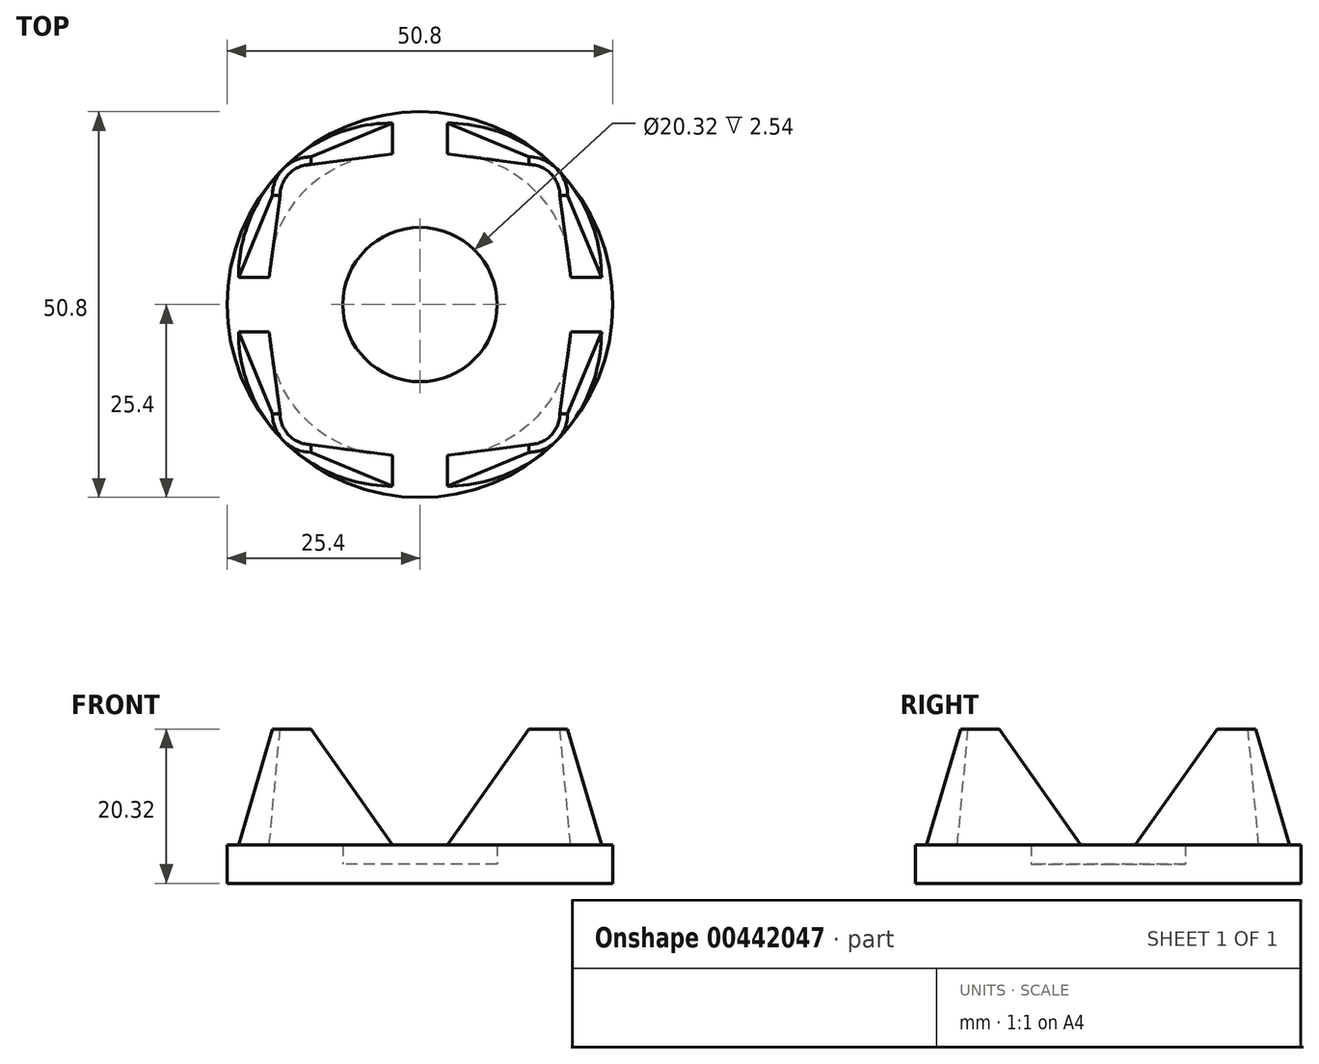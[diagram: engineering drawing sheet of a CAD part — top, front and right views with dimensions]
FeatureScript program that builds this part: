
annotation { "Feature Type Name" : "Feature", "Feature Type Description" : "" }
export const myFeature = defineFeature(function(context is Context, id is Id, definition is map)
    precondition{}
    {
        {
            var Q0;
            Q0=qCreatedBy(makeId("Top.planeOp"),FACE);
            var sketch = newSketch(context, id + "F0", { "sketchPlane" : qUnion([Q0])});
            skCircle(sketch, "E0", {"center": v(0, 0) * mm, "radius": 25.4 * mm});
            skCircle(sketch, "E1", {"center": v(0, 0) * mm, "radius": 10.16 * mm});
            skCircle(sketch, "E2.0", {"center": v(0, 0) * mm, "radius": 20.32 * mm});
            skLineSegment(sketch, "E3", {"start": v(0, 0) * mm, "end": v(0, 25.4) * mm});
            skLineSegment(sketch, "E4", {"start": v(0, 0) * mm, "end": v(-25.4, 0) * mm});
            skLineSegment(sketch, "E5", {"start": v(0, 0) * mm, "end": v(0, -25.4) * mm});
            skLineSegment(sketch, "E6", {"start": v(0, 0) * mm, "end": v(25.4, 0) * mm});
            skSolve(sketch);
        }
        {
            var Q0;
            Q0=makeQuery(id+"F0.imprint","IMPRINT",FACE,{"disambiguationData":[TD([[makeQuery(id+"F0.imprint","IMPRINT",EDGE,{"derivedFrom":sQuery(id+"F0.wireOp",EDGE,"E0")}),1.0]])]});
            var Q1;
            {var subQ0=sQuery(id+"F0.wireOp",EDGE,"E3");var subQ1=sQuery(id+"F0.wireOp",EDGE,"E2.0");var subQ2=makeQuery(id+"F0.imprint","INTERSECT",VERTEX,{"derivedFrom":[subQ1,subQ0]});Q1=makeQuery(id+"F0.imprint","IMPRINT",FACE,{"disambiguationData":[TD([[makeQuery(id+"F0.imprint","IMPRINT",EDGE,{"disambiguationData":[TD([[subQ2,-1.0]])],"derivedFrom":subQ1}),1.0]])]});}
            var Q2;
            {var subQ0=sQuery(id+"F0.wireOp",EDGE,"E3");var subQ1=sQuery(id+"F0.wireOp",EDGE,"E2.0");var subQ2=makeQuery(id+"F0.imprint","INTERSECT",VERTEX,{"derivedFrom":[subQ1,subQ0]});Q2=makeQuery(id+"F0.imprint","IMPRINT",FACE,{"disambiguationData":[TD([[makeQuery(id+"F0.imprint","IMPRINT",EDGE,{"disambiguationData":[TD([[subQ2,1.0]])],"derivedFrom":subQ1}),1.0]])]});}
            var Q3;
            {var subQ0=sQuery(id+"F0.wireOp",EDGE,"E5");var subQ1=sQuery(id+"F0.wireOp",EDGE,"E1");var subQ2=makeQuery(id+"F0.imprint","INTERSECT",VERTEX,{"derivedFrom":[subQ1,subQ0]});Q3=makeQuery(id+"F0.imprint","IMPRINT",FACE,{"disambiguationData":[TD([[makeQuery(id+"F0.imprint","IMPRINT",EDGE,{"disambiguationData":[TD([[subQ2,1.0]])],"derivedFrom":subQ1}),-1.0]])]});}
            var Q4;
            {var subQ0=sQuery(id+"F0.wireOp",EDGE,"E5");var subQ1=sQuery(id+"F0.wireOp",EDGE,"E1");var subQ2=makeQuery(id+"F0.imprint","INTERSECT",VERTEX,{"derivedFrom":[subQ1,subQ0]});Q4=makeQuery(id+"F0.imprint","IMPRINT",FACE,{"disambiguationData":[TD([[makeQuery(id+"F0.imprint","IMPRINT",EDGE,{"disambiguationData":[TD([[subQ2,-1.0]])],"derivedFrom":subQ1}),-1.0]])]});}
            extrude(context, id + "F1", {"entities" : qUnion([Q0, Q1, Q2, Q3, Q4]), "depth" : 5.08 * mm});
        }
        {
            var Q0;
            Q0=makeQuery(id+"F0.imprint","IMPRINT",FACE,{"disambiguationData":[TD([[makeQuery(id+"F0.imprint","IMPRINT",EDGE,{"derivedFrom":sQuery(id+"F0.wireOp",EDGE,"E1")}),1.0]])]});
            extrude(context, id + "F2", {"entities" : qUnion([Q0]), "operationType" : NewBodyOperationType.ADD, "depth" : 2.54 * mm});
        }
        {
            var Q0;
            Q0=qCreatedBy(makeId("Top.planeOp"),FACE);
            cPlane(context, id + "F3", {"entities" : qUnion([Q0]), "cplaneType" : CPlaneType.OFFSET, "offset" : 25.4 * mm, "width" : 152.4 * mm, "height" : 152.4 * mm});
        }
        {
            var Q0;
            Q0=qCreatedBy(id+"F3.planeOp",FACE);
            var sketch = newSketch(context, id + "F4", { "sketchPlane" : qUnion([Q0])});
            skCircle(sketch, "E7.cCircle", {"center": v(0, 0) * mm, "radius": 17.96 * mm, "construction": true});
            skLineSegment(sketch, "E7.0", {"start": v(-17.96, -17.96) * mm, "end": v(-17.96, 17.96) * mm});
            skLineSegment(sketch, "E7.1", {"start": v(-17.96, 17.96) * mm, "end": v(17.96, 17.96) * mm});
            skLineSegment(sketch, "E7.2", {"start": v(17.96, 17.96) * mm, "end": v(17.96, -17.96) * mm});
            skLineSegment(sketch, "E7.3", {"start": v(17.96, -17.96) * mm, "end": v(-17.96, -17.96) * mm});
            skPoint(sketch, "E7.0.midPoint", {"position": v(-17.96, 0) * mm});
            skSolve(sketch);
        }
        {
            var Q1;
            {var subQ0=sQuery(id+"F0.wireOp",EDGE,"E3");var subQ1=sQuery(id+"F0.wireOp",EDGE,"E0");var subQ2=makeQuery(id+"F0.imprint","INTERSECT",VERTEX,{"derivedFrom":[subQ1,subQ0]});Q1=makeQuery(id+"F0.imprint","IMPRINT",FACE,{"disambiguationData":[TD([[makeQuery(id+"F0.imprint","IMPRINT",EDGE,{"disambiguationData":[TD([[subQ2,-1.0]])],"derivedFrom":subQ1}),1.0]])]});}
            var Q2;
            Q2=sQuery(id+"F4.wireOp",VERTEX,"E7.1.start");
            loft(context, id + "F5", {"operationType" : NewBodyOperationType.ADD, "sheetProfilesArray" : [{ "sheetProfileEntities" : qUnion([Q1]) }, { "sheetProfileEntities" : qUnion([Q2]) }]});
        }
        {
            var Q1;
            {var subQ0=sQuery(id+"F0.wireOp",EDGE,"E4");var subQ1=sQuery(id+"F0.wireOp",EDGE,"E0");var subQ2=makeQuery(id+"F0.imprint","INTERSECT",VERTEX,{"derivedFrom":[subQ1,subQ0]});Q1=makeQuery(id+"F0.imprint","IMPRINT",FACE,{"disambiguationData":[TD([[makeQuery(id+"F0.imprint","IMPRINT",EDGE,{"disambiguationData":[TD([[subQ2,-1.0]])],"derivedFrom":subQ1}),1.0]])]});}
            var Q2;
            Q2=sQuery(id+"F4.wireOp",VERTEX,"E7.0.start");
            loft(context, id + "F6", {"operationType" : NewBodyOperationType.ADD, "sheetProfilesArray" : [{ "sheetProfileEntities" : qUnion([Q1]) }, { "sheetProfileEntities" : qUnion([Q2]) }]});
        }
        {
            var Q1;
            {var subQ0=sQuery(id+"F0.wireOp",EDGE,"E5");var subQ1=sQuery(id+"F0.wireOp",EDGE,"E0");var subQ2=makeQuery(id+"F0.imprint","INTERSECT",VERTEX,{"derivedFrom":[subQ1,subQ0]});Q1=makeQuery(id+"F0.imprint","IMPRINT",FACE,{"disambiguationData":[TD([[makeQuery(id+"F0.imprint","IMPRINT",EDGE,{"disambiguationData":[TD([[subQ2,-1.0]])],"derivedFrom":subQ1}),1.0]])]});}
            var Q2;
            Q2=sQuery(id+"F4.wireOp",VERTEX,"E7.3.start");
            loft(context, id + "F7", {"operationType" : NewBodyOperationType.ADD, "sheetProfilesArray" : [{ "sheetProfileEntities" : qUnion([Q1]) }, { "sheetProfileEntities" : qUnion([Q2]) }]});
        }
        {
            var Q1;
            {var subQ0=sQuery(id+"F0.wireOp",EDGE,"E3");var subQ1=sQuery(id+"F0.wireOp",EDGE,"E0");var subQ2=makeQuery(id+"F0.imprint","INTERSECT",VERTEX,{"derivedFrom":[subQ1,subQ0]});Q1=makeQuery(id+"F0.imprint","IMPRINT",FACE,{"disambiguationData":[TD([[makeQuery(id+"F0.imprint","IMPRINT",EDGE,{"disambiguationData":[TD([[subQ2,1.0]])],"derivedFrom":subQ1}),1.0]])]});}
            var Q2;
            Q2=sQuery(id+"F4.wireOp",VERTEX,"E7.2.start");
            loft(context, id + "F8", {"operationType" : NewBodyOperationType.ADD, "sheetProfilesArray" : [{ "sheetProfileEntities" : qUnion([Q1]) }, { "sheetProfileEntities" : qUnion([Q2]) }]});
        }
        {
            var Q0;
            Q0=qCreatedBy(id+"F3.planeOp",FACE);
            var sketch = newSketch(context, id + "F9", { "sketchPlane" : qUnion([Q0])});
            skCircle(sketch, "E8.cCircle", {"center": v(0, 0) * mm, "radius": 30.8 * mm, "construction": true});
            skLineSegment(sketch, "E8.0", {"start": v(-30.8, 30.8) * mm, "end": v(30.8, 30.8) * mm});
            skLineSegment(sketch, "E8.1", {"start": v(30.8, 30.8) * mm, "end": v(30.8, -30.8) * mm});
            skLineSegment(sketch, "E8.2", {"start": v(30.8, -30.8) * mm, "end": v(-30.8, -30.8) * mm});
            skLineSegment(sketch, "E8.3", {"start": v(-30.8, -30.8) * mm, "end": v(-30.8, 30.8) * mm});
            skPoint(sketch, "E8.0.midPoint", {"position": v(0, 30.8) * mm});
            skSolve(sketch);
        }
        {
            var Q0;
            Q0 = qSketchRegion(id + "F9", true);
            extrude(context, id + "F10", {"entities" : qUnion([Q0]), "operationType" : NewBodyOperationType.REMOVE, "oppositeDirection" : true, "depth" : 5.08 * mm});
        }
    });
